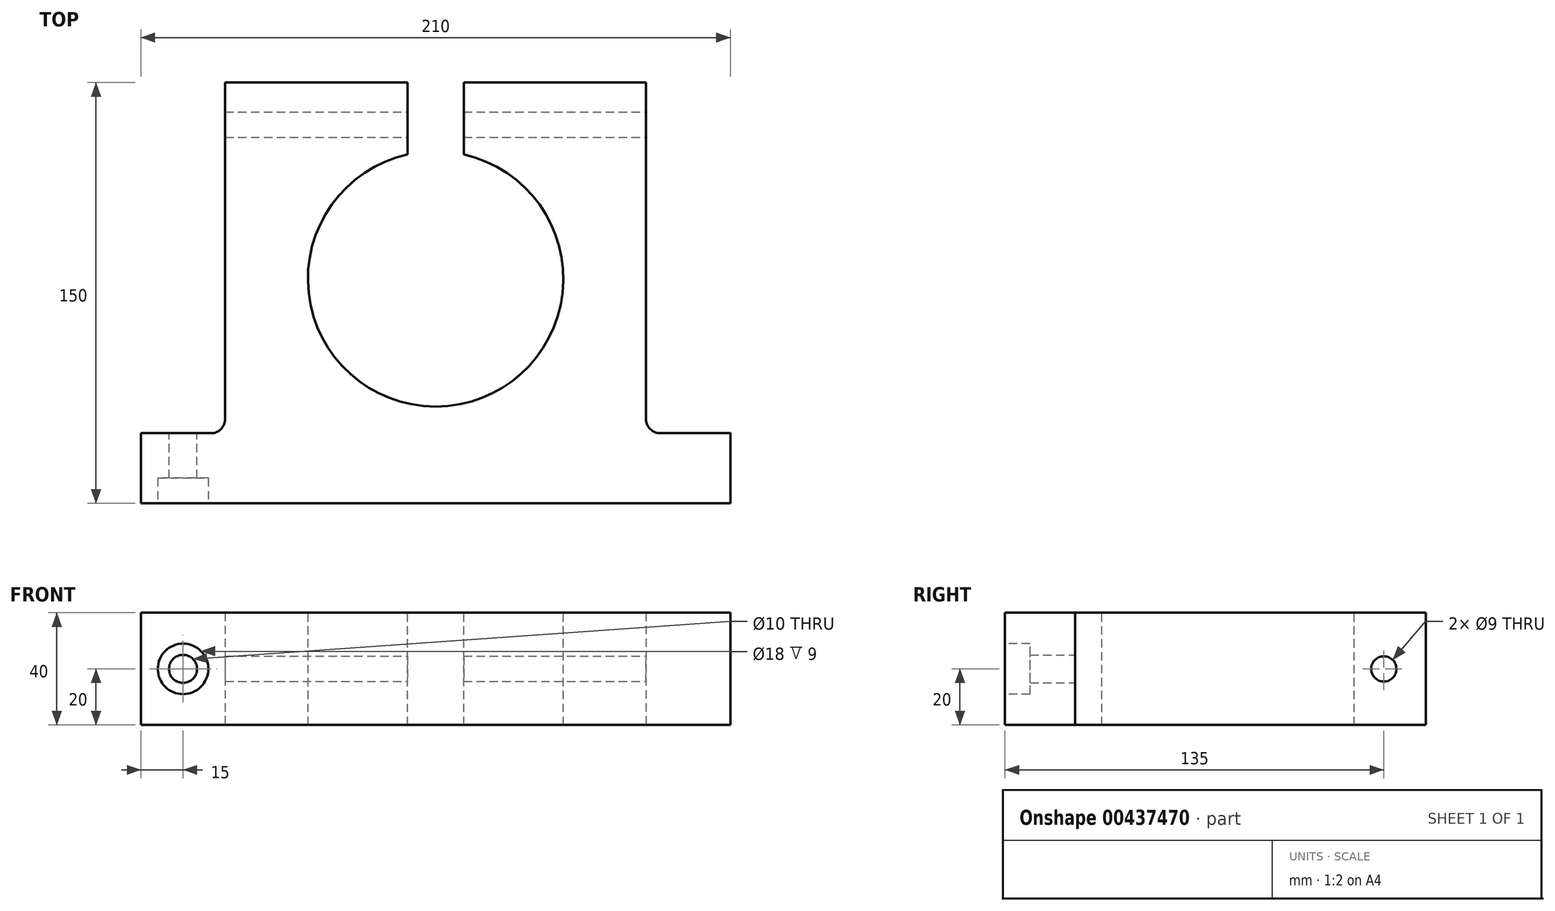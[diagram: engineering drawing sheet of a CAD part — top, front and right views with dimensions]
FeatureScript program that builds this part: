
annotation { "Feature Type Name" : "Feature", "Feature Type Description" : "" }
export const myFeature = defineFeature(function(context is Context, id is Id, definition is map)
    precondition{}
    {
        {
            var Q0;
            Q0=qCreatedBy(makeId("Top.planeOp"),FACE);
            var sketch = newSketch(context, id + "F0", { "sketchPlane" : qUnion([Q0])});
            skLineSegment(sketch, "E0", {"start": v(-105, 0) * mm, "end": v(-105, 25) * mm});
            skLineSegment(sketch, "E1", {"start": v(-105, 25) * mm, "end": v(-75, 25) * mm});
            skLineSegment(sketch, "E2", {"start": v(-75, 25) * mm, "end": v(-75, 150) * mm});
            skLineSegment(sketch, "E3", {"start": v(-75, 150) * mm, "end": v(75, 150) * mm});
            skLineSegment(sketch, "E4", {"start": v(75, 150) * mm, "end": v(75, 25) * mm});
            skLineSegment(sketch, "E5", {"start": v(75, 25) * mm, "end": v(105, 25) * mm});
            skLineSegment(sketch, "E6", {"start": v(105, 25) * mm, "end": v(105, 0) * mm});
            skLineSegment(sketch, "E7", {"start": v(105, 0) * mm, "end": v(-105, 0) * mm});
            skSolve(sketch);
        }
        {
            var Q0;
            Q0=makeQuery(id+"F0.imprint","IMPRINT",FACE,{"disambiguationData":[TD([[makeQuery(id+"F0.imprint","IMPRINT",EDGE,{"derivedFrom":sQuery(id+"F0.wireOp",EDGE,"E0")}),-1.0]])]});
            extrude(context, id + "F1", {"entities" : qUnion([Q0]), "depth" : 40 * mm});
        }
        {
            var Q0;
            Q0=makeQuery(id+"F1.opExtrude","CAP_FACE",FACE,{"disambiguationData":[OSD([sQuery(id+"F0.wireOp",EDGE,"E0"),sQuery(id+"F0.wireOp",EDGE,"E1"),sQuery(id+"F0.wireOp",EDGE,"E2"),sQuery(id+"F0.wireOp",EDGE,"E3"),sQuery(id+"F0.wireOp",EDGE,"E4"),sQuery(id+"F0.wireOp",EDGE,"E5"),sQuery(id+"F0.wireOp",EDGE,"E6"),sQuery(id+"F0.wireOp",EDGE,"E7")])],"isStart":false});
            var sketch = newSketch(context, id + "F2", { "sketchPlane" : qUnion([Q0])});
            skCircle(sketch, "E8", {"center": v(0, 80) * mm, "radius": 45.5 * mm});
            skSolve(sketch);
        }
        {
            var Q0;
            Q0 = qSketchRegion(id + "F2", true);
            extrude(context, id + "F3", {"entities" : qUnion([Q0]), "operationType" : NewBodyOperationType.REMOVE, "endBound" : BoundingType.THROUGH_ALL, "oppositeDirection" : true, "depth" : 25 * mm});
        }
        {
            var Q0;
            Q0=makeQuery(id+"F1.opExtrude","CAP_FACE",FACE,{"disambiguationData":[OSD([sQuery(id+"F0.wireOp",EDGE,"E0"),sQuery(id+"F0.wireOp",EDGE,"E1"),sQuery(id+"F0.wireOp",EDGE,"E2"),sQuery(id+"F0.wireOp",EDGE,"E3"),sQuery(id+"F0.wireOp",EDGE,"E4"),sQuery(id+"F0.wireOp",EDGE,"E5"),sQuery(id+"F0.wireOp",EDGE,"E6"),sQuery(id+"F0.wireOp",EDGE,"E7")])],"isStart":false});
            var sketch = newSketch(context, id + "F4", { "sketchPlane" : qUnion([Q0])});
            skLineSegment(sketch, "E9.bottom", {"start": v(-10, 150) * mm, "end": v(10, 150) * mm});
            skLineSegment(sketch, "E9.top", {"start": v(-10, 124.39) * mm, "end": v(10, 124.39) * mm});
            skLineSegment(sketch, "E9.left", {"start": v(-10, 150) * mm, "end": v(-10, 124.39) * mm});
            skLineSegment(sketch, "E9.right", {"start": v(10, 150) * mm, "end": v(10, 124.39) * mm});
            skSolve(sketch);
        }
        {
            var Q0;
            Q0 = qSketchRegion(id + "F4", true);
            extrude(context, id + "F5", {"entities" : qUnion([Q0]), "operationType" : NewBodyOperationType.REMOVE, "endBound" : BoundingType.THROUGH_ALL, "oppositeDirection" : true, "depth" : 25 * mm});
        }
        {
            var Q0;
            Q0=makeQuery(id+"F1.opExtrude","SWEPT_FACE",FACE,{"disambiguationData":[OSD([sQuery(id+"F0.wireOp",EDGE,"E4")])]});
            var sketch = newSketch(context, id + "F6", { "sketchPlane" : qUnion([Q0])});
            skCircle(sketch, "E10", {"center": v(135, 20) * mm, "radius": 4.5 * mm});
            skPoint(sketch, "E10.centerSnap0", {"position": v(150, 20) * mm});
            skSolve(sketch);
        }
        {
            var Q0;
            Q0 = qSketchRegion(id + "F6", true);
            extrude(context, id + "F7", {"entities" : qUnion([Q0]), "operationType" : NewBodyOperationType.REMOVE, "endBound" : BoundingType.THROUGH_ALL, "oppositeDirection" : true, "depth" : 25 * mm});
        }
        {
            var Q0;
            Q0=makeQuery(id+"F1.opExtrude","SWEPT_FACE",FACE,{"disambiguationData":[OSD([sQuery(id+"F0.wireOp",EDGE,"E1")])]});
            var sketch = newSketch(context, id + "F8", { "sketchPlane" : qUnion([Q0])});
            skCircle(sketch, "E11", {"center": v(90, 20) * mm, "radius": 5 * mm});
            skSolve(sketch);
        }
        {
            var Q0;
            Q0 = qSketchRegion(id + "F8", true);
            extrude(context, id + "F9", {"entities" : qUnion([Q0]), "operationType" : NewBodyOperationType.REMOVE, "endBound" : BoundingType.THROUGH_ALL, "oppositeDirection" : true, "depth" : 25 * mm});
        }
        {
            var Q0;
            Q0=makeQuery(id+"F1.opExtrude","SWEPT_FACE",FACE,{"disambiguationData":[OSD([sQuery(id+"F0.wireOp",EDGE,"E7")])]});
            var sketch = newSketch(context, id + "F10", { "sketchPlane" : qUnion([Q0])});
            skCircle(sketch, "E12", {"center": v(-90, 20) * mm, "radius": 9 * mm});
            skSolve(sketch);
        }
        {
            var Q0;
            Q0=makeQuery(id+"F10.imprint","IMPRINT",FACE,{"disambiguationData":[TD([[makeQuery(id+"F10.imprint","IMPRINT",EDGE,{"derivedFrom":sQuery(id+"F10.wireOp",EDGE,"E12")}),1.0]])]});
            extrude(context, id + "F11", {"entities" : qUnion([Q0]), "operationType" : NewBodyOperationType.REMOVE, "oppositeDirection" : true, "depth" : 9 * mm});
        }
        {
            var Q0;
            Q0=makeQuery(id+"F1.opExtrude","SWEPT_EDGE",EDGE,{"disambiguationData":[OSD([sQuery(id+"F0.wireOp",EDGE,"E1"),sQuery(id+"F0.wireOp",EDGE,"E2")])]});
            var Q1;
            Q1=makeQuery(id+"F1.opExtrude","SWEPT_EDGE",EDGE,{"disambiguationData":[OSD([sQuery(id+"F0.wireOp",EDGE,"E4"),sQuery(id+"F0.wireOp",EDGE,"E5")])]});
            fillet(context, id + "F12", {"entities" : qUnion([Q0, Q1]), "radius" : 5 * mm, "tangentPropagation" : true, "allowEdgeOverflow" : false});
        }
    });
